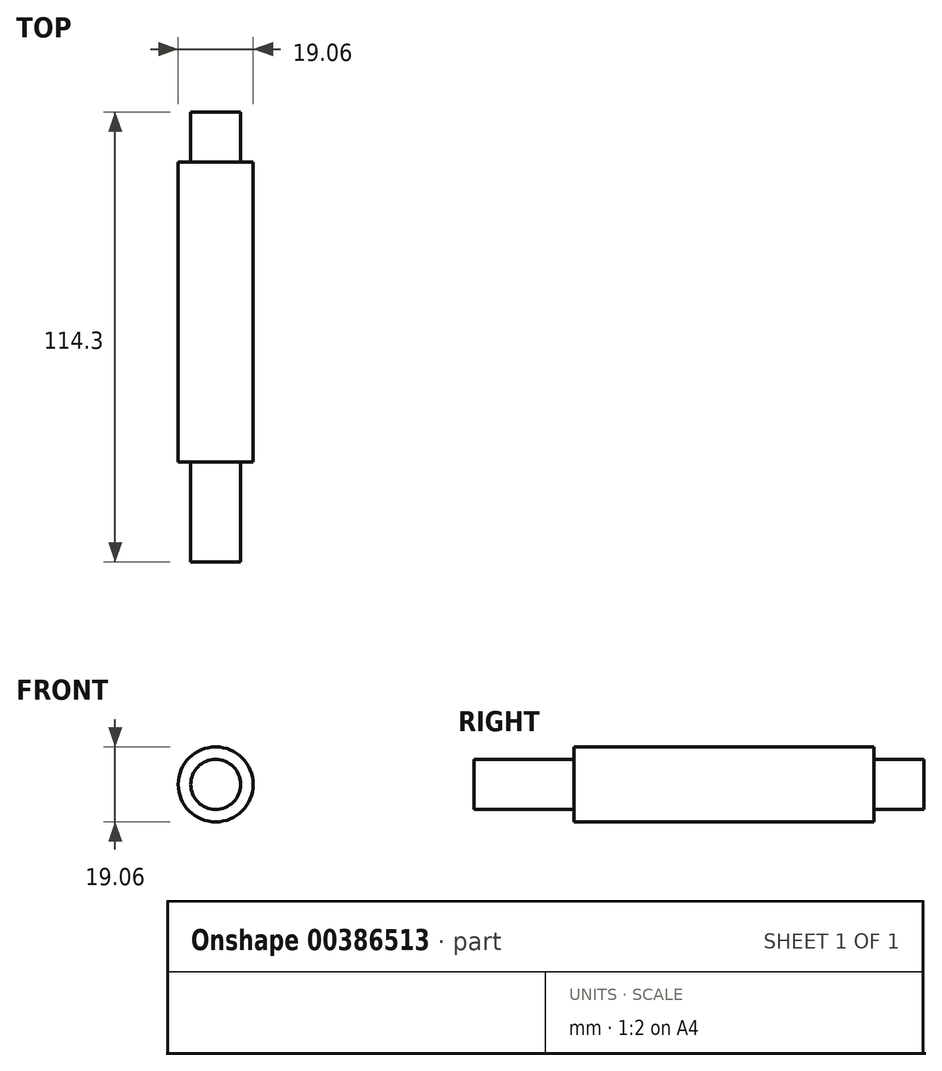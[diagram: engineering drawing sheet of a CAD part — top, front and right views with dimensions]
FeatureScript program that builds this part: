
annotation { "Feature Type Name" : "Feature", "Feature Type Description" : "" }
export const myFeature = defineFeature(function(context is Context, id is Id, definition is map)
    precondition{}
    {
        {
            var Q0;
            Q0=qCreatedBy(makeId("Front.planeOp"),FACE);
            var sketch = newSketch(context, id + "F0", { "sketchPlane" : qUnion([Q0])});
            skCircle(sketch, "E0", {"center": v(0, 0) * mm, "radius": 6.35 * mm});
            skSolve(sketch);
        }
        {
            var Q0;
            Q0=makeQuery(id+"F0.imprint","IMPRINT",FACE,{"disambiguationData":[TD([[makeQuery(id+"F0.imprint","IMPRINT",EDGE,{"derivedFrom":sQuery(id+"F0.wireOp",EDGE,"E0")}),1.0]])]});
            extrude(context, id + "F1", {"entities" : qUnion([Q0]), "depth" : 25.4 * mm});
        }
        {
            var Q0;
            Q0=qCreatedBy(makeId("Front.planeOp"),FACE);
            var sketch = newSketch(context, id + "F2", { "sketchPlane" : qUnion([Q0])});
            skCircle(sketch, "E1", {"center": v(0, 0) * mm, "radius": 9.53 * mm});
            skSolve(sketch);
        }
        {
            var Q0;
            Q0=makeQuery(id+"F2.imprint","IMPRINT",FACE,{"disambiguationData":[TD([[makeQuery(id+"F2.imprint","IMPRINT",EDGE,{"derivedFrom":sQuery(id+"F2.wireOp",EDGE,"E1")}),1.0]])]});
            var Q1;
            Q1 = qSketchRegion(id + "FljG47cBei8NBg5_1", true);
            extrude(context, id + "F3", {"entities" : qUnion([Q0, Q1]), "operationType" : NewBodyOperationType.ADD, "oppositeDirection" : true, "depth" : 76.2 * mm});
        }
        {
            var Q0;
            Q0=makeQuery(id+"F3.opExtrude","CAP_FACE",FACE,{"disambiguationData":[OSD([sQuery(id+"F2.wireOp",EDGE,"E1")])],"isStart":false});
            var sketch = newSketch(context, id + "F4", { "sketchPlane" : qUnion([Q0])});
            skCircle(sketch, "E2", {"center": v(0, 0) * mm, "radius": 6.35 * mm});
            skSolve(sketch);
        }
        {
            var Q0;
            Q0=makeQuery(id+"F4.imprint","IMPRINT",FACE,{"disambiguationData":[TD([[makeQuery(id+"F4.imprint","IMPRINT",EDGE,{"derivedFrom":sQuery(id+"F4.wireOp",EDGE,"E2")}),1.0]])]});
            extrude(context, id + "F5", {"entities" : qUnion([Q0]), "operationType" : NewBodyOperationType.ADD, "depth" : 12.7 * mm});
        }
    });
